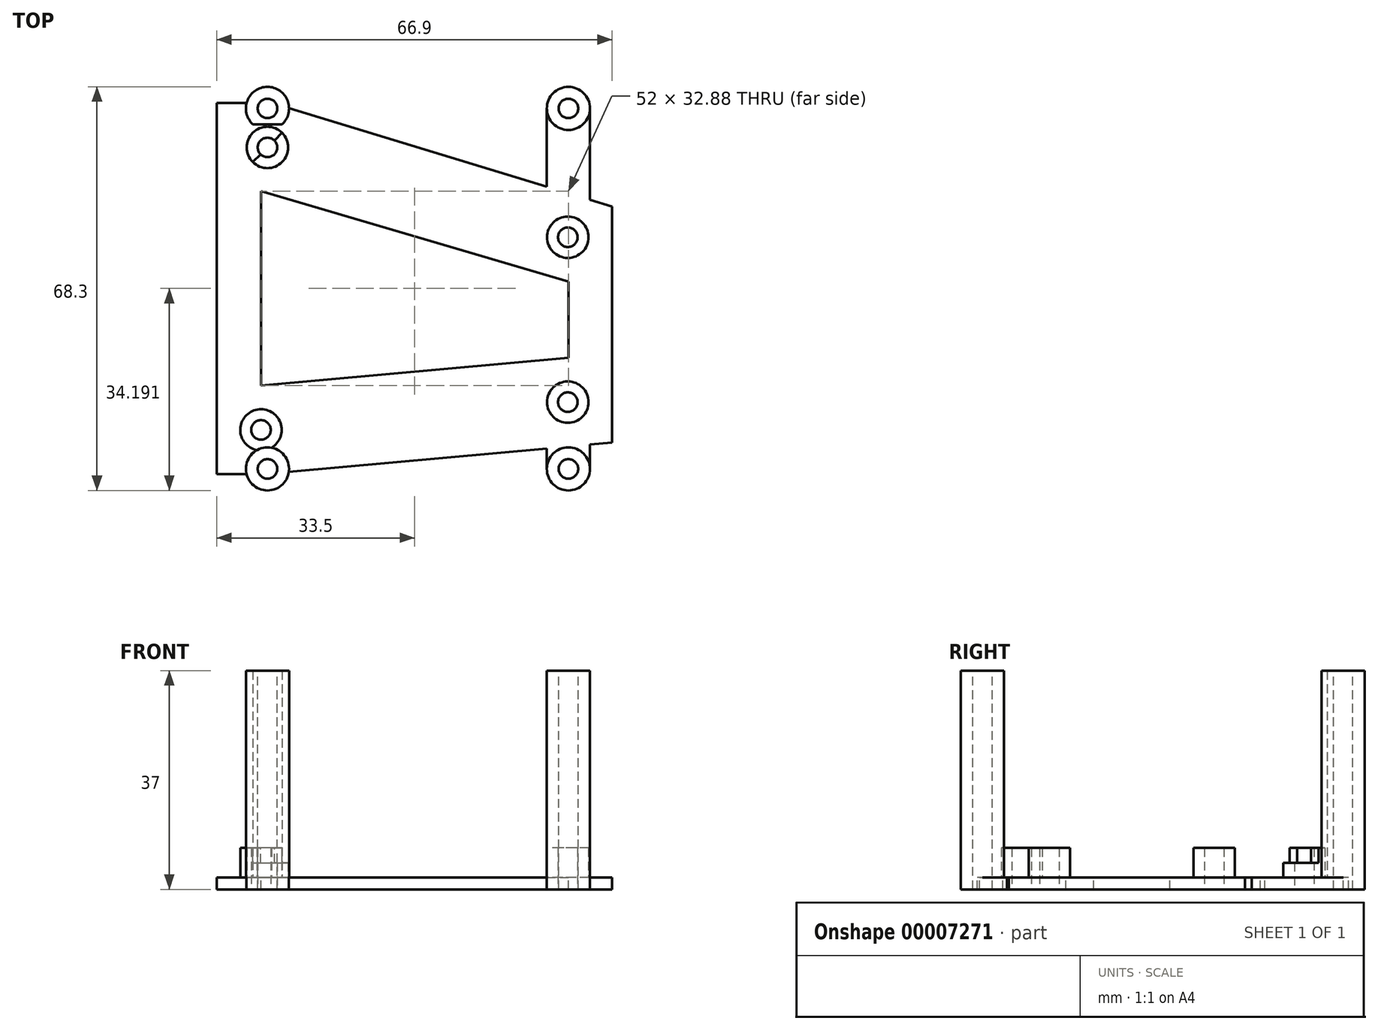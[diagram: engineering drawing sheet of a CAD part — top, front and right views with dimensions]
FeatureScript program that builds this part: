
annotation { "Feature Type Name" : "Feature", "Feature Type Description" : "" }
export const myFeature = defineFeature(function(context is Context, id is Id, definition is map)
    precondition{}
    {
        {
            var Q0;
            Q0=qCreatedBy(makeId("Top.planeOp"),FACE);
            var sketch = newSketch(context, id + "F0", { "sketchPlane" : qUnion([Q0])});
            skCircle(sketch, "E0", {"center": v(0, 0) * mm, "radius": 1.65 * mm});
            skCircle(sketch, "E1", {"center": v(51.9, 4.7) * mm, "radius": 1.65 * mm});
            skCircle(sketch, "E2", {"center": v(51.9, 32.6) * mm, "radius": 1.65 * mm});
            skCircle(sketch, "E3", {"center": v(1.1, 47.8) * mm, "radius": 1.65 * mm});
            skCircle(sketch, "E4", {"center": v(1.1, 47.8) * mm, "radius": 3.5 * mm});
            skCircle(sketch, "E5", {"center": v(51.9, 32.6) * mm, "radius": 3.5 * mm});
            skCircle(sketch, "E6", {"center": v(51.9, 4.7) * mm, "radius": 3.5 * mm});
            skCircle(sketch, "E7", {"center": v(0, 0) * mm, "radius": 3.5 * mm});
            skSolve(sketch);
        }
        {
            var Q0;
            Q0 = qSketchRegion(id + "F0", true);
            extrude(context, id + "F1", {"entities" : qUnion([Q0]), "depth" : 5 * mm});
        }
        {
            var Q0;
            Q0=qCreatedBy(makeId("Top.planeOp"),FACE);
            var sketch = newSketch(context, id + "F2", { "sketchPlane" : qUnion([Q0])});
            skLineSegment(sketch, "E8.rect.bottom", {"start": v(-2.44, 55.3) * mm, "end": v(-7.5, 55.3) * mm});
            skLineSegment(sketch, "E8.rect.top", {"start": v(0.34, -7.5) * mm, "end": v(-7.5, -7.5) * mm});
            skLineSegment(sketch, "E8.rect.left", {"start": v(59.4, 37.8) * mm, "end": v(59.4, -2.15) * mm});
            skLineSegment(sketch, "E8.rect.right", {"start": v(-7.5, 55.3) * mm, "end": v(-7.5, -7.5) * mm});
            skPoint(sketch, "E8.rect.middle", {"position": v(25.95, 23.9) * mm});
            skLineSegment(sketch, "E9", {"start": v(0, 7.5) * mm, "end": v(52, 12.2) * mm});
            skLineSegment(sketch, "E10", {"start": v(52, 12.2) * mm, "end": v(52, 25.1) * mm});
            skLineSegment(sketch, "E11", {"start": v(52, 25.1) * mm, "end": v(0, 40.38) * mm});
            skLineSegment(sketch, "E12", {"start": v(0, 40.38) * mm, "end": v(0, 7.5) * mm});
            skLineSegment(sketch, "E13", {"start": v(59.4, -2.15) * mm, "end": v(55.65, -2.5) * mm});
            skPoint(sketch, "E14.orphan", {"position": v(59.4, -7.5) * mm});
            skPoint(sketch, "E15.orphan", {"position": v(59.4, 55.3) * mm});
            skCircle(sketch, "E16.0", {"center": v(0, 0) * mm, "radius": 1.65 * mm});
            skCircle(sketch, "E16.1", {"center": v(51.9, 4.7) * mm, "radius": 1.65 * mm});
            skCircle(sketch, "E16.2", {"center": v(51.9, 32.6) * mm, "radius": 1.65 * mm});
            skCircle(sketch, "E16.3", {"center": v(1.1, 47.8) * mm, "radius": 1.65 * mm});
            skLineSegment(sketch, "E17", {"start": v(0, -6.6) * mm, "end": v(52, -6.6) * mm, "construction": true});
            skLineSegment(sketch, "E18", {"start": v(52, -6.6) * mm, "end": v(52, 54.4) * mm, "construction": true});
            skLineSegment(sketch, "E19", {"start": v(52, 54.4) * mm, "end": v(1.1, 54.4) * mm, "construction": true});
            skLineSegment(sketch, "E20", {"start": v(1.1, 54.4) * mm, "end": v(1.1, 47.8) * mm, "construction": true});
            skLineSegment(sketch, "E21", {"start": v(0, -6.6) * mm, "end": v(0, 0) * mm, "construction": true});
            skLineSegment(sketch, "E22", {"start": v(1.1, 47.8) * mm, "end": v(1.1, -6.6) * mm, "construction": true});
            skCircle(sketch, "E23", {"center": v(1.1, -6.6) * mm, "radius": 1.65 * mm});
            skCircle(sketch, "E24", {"center": v(52, -6.6) * mm, "radius": 1.65 * mm});
            skCircle(sketch, "E25", {"center": v(52, 54.4) * mm, "radius": 1.65 * mm});
            skCircle(sketch, "E26", {"center": v(1.1, 54.4) * mm, "radius": 1.65 * mm});
            skArc(sketch, "E27", {"start": v(4.75, 54.45) * mm, "mid": v(1.53, 58.02) * mm, "end": v(-2.44, 55.3) * mm});
            skArc(sketch, "E28", {"start": v(55.65, 54.4) * mm, "mid": v(52, 58.05) * mm, "end": v(48.35, 54.4) * mm});
            skArc(sketch, "E29", {"start": v(48.35, -6.6) * mm, "mid": v(52, -10.25) * mm, "end": v(55.65, -6.6) * mm});
            skArc(sketch, "E30", {"start": v(-2.44, -7.5) * mm, "mid": v(1.3, -10.24) * mm, "end": v(4.72, -7.1) * mm});
            skLineSegment(sketch, "E31.trimOffspring", {"start": v(48.35, -3.15) * mm, "end": v(0.34, -7.5) * mm});
            skLineSegment(sketch, "E32", {"start": v(48.35, -3.15) * mm, "end": v(48.35, -6.6) * mm});
            skLineSegment(sketch, "E33", {"start": v(55.65, -6.6) * mm, "end": v(55.65, -2.5) * mm});
            skLineSegment(sketch, "E34", {"start": v(55.65, 54.4) * mm, "end": v(55.65, 38.95) * mm});
            skLineSegment(sketch, "E35", {"start": v(48.35, 54.4) * mm, "end": v(48.35, 41.17) * mm});
            skLineSegment(sketch, "E36.trimOffspring", {"start": v(4.75, 54.45) * mm, "end": v(48.35, 41.17) * mm});
            skLineSegment(sketch, "E37.trimOffspring", {"start": v(55.65, 38.95) * mm, "end": v(59.4, 37.8) * mm});
            skLineSegment(sketch, "E38", {"start": v(1.1, 47.8) * mm, "end": v(51.9, 32.6) * mm, "construction": true});
            skSolve(sketch);
        }
        {
            var Q0;
            Q0 = qSketchRegion(id + "F2", true);
            extrude(context, id + "F3", {"entities" : qUnion([Q0]), "operationType" : NewBodyOperationType.ADD, "oppositeDirection" : true, "depth" : 2 * mm});
        }
        {
            var Q0;
            Q0=makeQuery(id+"F1.opExtrude","CAP_FACE",FACE,{"disambiguationData":[OSD([sQuery(id+"F0.wireOp",EDGE,"E3"),sQuery(id+"F0.wireOp",EDGE,"E4")])],"isStart":false});
            var sketch = newSketch(context, id + "F4", { "sketchPlane" : qUnion([Q0])});
            skLineSegment(sketch, "E39", {"start": v(-1.37, 45.33) * mm, "end": v(-0.07, 46.63) * mm});
            skArc(sketch, "E40.0", {"start": v(-1.37, 45.33) * mm, "mid": v(3.57, 45.33) * mm, "end": v(3.57, 50.27) * mm});
            skArc(sketch, "E41.0", {"start": v(-0.07, 46.63) * mm, "mid": v(2.27, 46.63) * mm, "end": v(2.27, 48.97) * mm});
            skLineSegment(sketch, "E42.trimOffspring", {"start": v(2.27, 48.97) * mm, "end": v(3.57, 50.27) * mm});
            skSolve(sketch);
        }
        {
            var Q0;
            Q0 = qSketchRegion(id + "F4", true);
            extrude(context, id + "F5", {"entities" : qUnion([Q0]), "operationType" : NewBodyOperationType.REMOVE, "oppositeDirection" : true, "depth" : 2.5 * mm});
        }
        {
            var Q0;
            Q0=makeQuery(id+"F3.opExtrude","CAP_FACE",FACE,{"disambiguationData":[OSD([sQuery(id+"F2.wireOp",EDGE,"E8.rect.bottom"),sQuery(id+"F2.wireOp",EDGE,"E8.rect.top"),sQuery(id+"F2.wireOp",EDGE,"E8.rect.left"),sQuery(id+"F2.wireOp",EDGE,"E8.rect.right"),sQuery(id+"F2.wireOp",EDGE,"E9"),sQuery(id+"F2.wireOp",EDGE,"E10"),sQuery(id+"F2.wireOp",EDGE,"E11"),sQuery(id+"F2.wireOp",EDGE,"E12"),sQuery(id+"F2.wireOp",EDGE,"E13"),sQuery(id+"F2.wireOp",EDGE,"E16.0"),sQuery(id+"F2.wireOp",EDGE,"E16.1"),sQuery(id+"F2.wireOp",EDGE,"E16.2"),sQuery(id+"F2.wireOp",EDGE,"E16.3"),sQuery(id+"F2.wireOp",EDGE,"E23"),sQuery(id+"F2.wireOp",EDGE,"E24"),sQuery(id+"F2.wireOp",EDGE,"E25"),sQuery(id+"F2.wireOp",EDGE,"E26"),sQuery(id+"F2.wireOp",EDGE,"E27"),sQuery(id+"F2.wireOp",EDGE,"E28"),sQuery(id+"F2.wireOp",EDGE,"E29"),sQuery(id+"F2.wireOp",EDGE,"E30"),sQuery(id+"F2.wireOp",EDGE,"E31.trimOffspring"),sQuery(id+"F2.wireOp",EDGE,"E32"),sQuery(id+"F2.wireOp",EDGE,"E33"),sQuery(id+"F2.wireOp",EDGE,"E34"),sQuery(id+"F2.wireOp",EDGE,"E35"),sQuery(id+"F2.wireOp",EDGE,"E36.trimOffspring"),sQuery(id+"F2.wireOp",EDGE,"E37.trimOffspring")])],"isStart":true});
            var sketch = newSketch(context, id + "F6", { "sketchPlane" : qUnion([Q0])});
            skCircle(sketch, "E43.0", {"center": v(1.1, 54.4) * mm, "radius": 1.65 * mm});
            skCircle(sketch, "E43.1", {"center": v(52, 54.4) * mm, "radius": 1.65 * mm});
            skCircle(sketch, "E43.2", {"center": v(52, -6.6) * mm, "radius": 1.65 * mm});
            skCircle(sketch, "E43.3", {"center": v(1.1, -6.6) * mm, "radius": 1.65 * mm});
            skCircle(sketch, "E44", {"center": v(52, 54.4) * mm, "radius": 3.65 * mm});
            skCircle(sketch, "E45", {"center": v(52, -6.6) * mm, "radius": 3.65 * mm});
            skCircle(sketch, "E46", {"center": v(1.1, -6.6) * mm, "radius": 3.65 * mm});
            skArc(sketch, "E47", {"start": v(3.56, 51.7) * mm, "mid": v(1.1, 58.05) * mm, "end": v(-1.36, 51.7) * mm});
            skLineSegment(sketch, "E48", {"start": v(-1.36, 51.7) * mm, "end": v(3.56, 51.7) * mm});
            skSolve(sketch);
        }
        {
            var Q0;
            Q0 = qSketchRegion(id + "F6", true);
            extrude(context, id + "F7", {"entities" : qUnion([Q0]), "operationType" : NewBodyOperationType.ADD, "depth" : 35 * mm});
        }
    });
